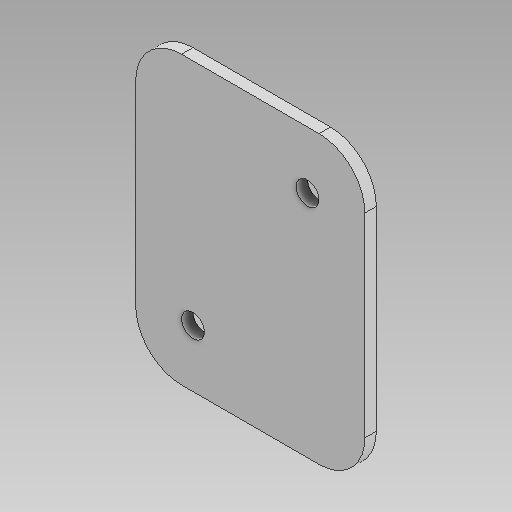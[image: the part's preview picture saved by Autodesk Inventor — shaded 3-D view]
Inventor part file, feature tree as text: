
AUTODESK INVENTOR PART (.ipt)
format: ipt  version: 2025 (Build 290162000, 162)  size: 102,912 bytes
history: native  units: in
note: dims shown in document units (in); Inventor stores cm internally (conversion verified against a paired STEP export)
features: other x1, extrude x1, sketch x1
ambient origin geometry x8: Origin, YZ Plane, XZ Plane, XY Plane, X Axis, Y Axis, Z Axis, Center Point
bodies: Body1 (feature_tree)
feature tree (3):
  other  "솔리드1"
  extrude  "돌출1"  Depth=0.3937in
  sketch  "스케치1"
